# Revit family: QF_ELECTROLUXPROFESSIONAL_1L059Y_TD6-14_E
name_source: partatom
category: Attrezzature speciali
units: mm (PartAtom-declared; Revit-internal decimal feet)

## family parameters
Basato su piano di lavoro = No
Condiviso = No
Punto di calcolo locali = No
Quota connettore circolare = Usa diametro
Sempre verticale = Sì
Taglio con vuoti quando caricato = No
Tipo di parte = Normale

## types (85) — shared parameters
Depth Actual = 965 mm  [stored 3.16601 ft]
Height Actual = 1771 mm  [stored 5.81037 ft]
Latent Heat Output = 0.0
Length Actual = 790 mm  [stored 2.59186 ft]
Modello = TD6-14
Produttore = Electrolux Professional
Sensible Heat Output = 0.0
URL = www.electroluxprofessional.com
Weight = 222
zero-valued in all types: Gas KW, Prospetto di default, Steam Pounds per Hour

## per-type parameters (varying)
| type | Cycle | Descrizione | Item Number | Phase | Volts | Watts |
| 9873730095 | 50 Hz | TUMBLE DRYER TD6-14 MARINE 14KG SST DRUM EL 13,5KW 400/50/3N COMPASS PRO 6G81 EU SILVER DO.LEFT.INS. MB DSC AFC STOP DIS | 1LSNF8 | 3 | 400 V | 14500 W |
| 9873730045 | 60 Hz | TUMBLE DRYER TD6-14 MARINE 14KG GALVA.DRUM EL 9KW 440/60/3 COMPASS PRO 6G82 SE SILVER DO.LEFT STOP DISCON. | 1L0EFV | 3 | 440 V | 10000 W |
| 9873730065 | 50 Hz | TUMBLE DRYER TD6-14 14KG GALVA.DRUM EL 13,5KW 400/50/3N COMPASS PRO 6G81 EU SILVER DO.RIGHT MB STOP DISCON. | 1L80FS | 3 | 400 V | 14500 W |
| 9873730075 | 50 Hz | TUMBLE DRYER TD6-14 14KG SST DRUM EL 13,5KW 400/50/3 COMPASS PRO 6L80 EU SILVER DO.RIGHT EXT.PM. DISCON. 2.I/O | 1L80GL | 3 | 400 V | 14500 W |
| 9873730161 | 50 Hz | TUMBLE DRYER TD6-14 14KG SST DRUM EL 9KW 400/50/3 COMPASS PRO 6L80 EU SILVER DO.RIGHT ELS-NETW. DISCON. 2.I/O | 1L0GDJ | 3 | 400 V | 10000 W |
| 9873730210 | 50 Hz | TUMBLE DRYER TD6-14 14KG SST DRUM EL 13,5KW 230/50/3 COMPASS PRO 6G81 EU SILVER DO.RIGHT MB STOP DISCON. | 1L0HEK | 3 | 230 V | 14600 W |
| 9873730111 | 60 Hz | TUMBLE DRYER TD6-14 14KG SST DRUM EL 13,5KW 230/60/3 COMPASS PRO 6G82 EU SILVER DO.RIGHT STOP DISCON. | 1LSNR6 | 3 | 230 V | 14600 W |
| 9873730131 | 50 Hz | TUMBLE DRYER TD6-14 MARINE 14KG SST DRUM EL 13,5KW 400/50/3 COMPASS PRO 6G82 EU SILVER DO.RIGHT STOP DISCON. | 1L0G28 | 3 | 400 V | 14500 W |
| 9873730081 | 50 Hz | TUMBLE DRYER TD6-14 MARINE 14KG GALVA.DRUM EL 13,5KW 400/50/3 COMPASS PRO 6G82 EU SILVER DO.RIGHT STOP DISCON. | 1LSN4T | 3 | 400 V | 14500 W |
| 9873730091 | 60 Hz | TUMBLE DRYER TD6-14 MARINE 14KG SST DRUM EL 13,5KW 440/60/3 COMPASS PRO 6G82 EU SILVER DO.LEFT STOP DISCON. | 1L0ELU | 3 | 440 V | 14500 W |
| 9873730194 | 60 Hz | TUMBLE DRYER TD6-14 MARINE 14KG SST DRUM EL 13,5KW 480/60/3 COMPASS PRO 6G82 EU SST DO.LEFT STOP DISCON. EXT.CONN. | 1LSPPY | 3 | 480 V | 14500 W |
| 9873730061 | 50 Hz | TUMBLE DRYER TD6-14 14KG SST DRUM EL 13,5KW 230/50/3 COMPASS PRO 6G82 EU SILVER DO.RIGHT STOP DISCON. | 1L80EJ | 3 | 230 V | 14600 W |
| 9873730071 | 50 Hz | TUMBLE DRYER TD6-14 14KG GALVA.DRUM EL 6KW 230/50/1N COMPASS PRO 6G81 EU SILVER DO.RIGHT MB STOP DISCON. | 1L0EJ0 | 1 | 230 V | 7000 W |
| 9873730011 | 50 Hz | TUMBLE DRYER TD6-14 14KG GALVA.DRUM EL 9KW 400/50/3N COMPASS PRO 6A81 SE SILVER DO.LEFT.INS. MB DISCON. EXT.CONN. | 1L0EE0 | 3 | 400 V | 10000 W |
| 9873730021 | 60 Hz | TUMBLE DRYER TD6-14 14KG GALVA.DRUM EL 13,5KW 440/60/3 COMPASS PRO 6G82 EU SST/SILVER DO.RIGHT.INS. STOP DISCON. | 1LSN3B | 3 | 440 V | 14500 W |
| 9873730154 | 50 Hz | TUMBLE DRYER TD6-14 14KG SST DRUM EL 13,5KW 400/50/3N COMPASS PRO 6L80 EU SILVER DO.RIGHT EXT.PM. DISCON. 2.I/O | 1LSPA9 | 3 | 400 V | 14500 W |
| 9873730164 | 50 Hz | TUMBLE DRYER TD6-14 14KG GALVA.DRUM EL 13,5KW 400/50/3N COMPASS PRO 6G82 EU SILVER DO.RIGHT AFC STOP DISCON. | 1L0GF2 | 3 | 400 V | 14500 W |
| 9873730174 | 60 Hz | TUMBLE DRYER TD6-14 14KG GALVA.DRUM EL 13,5KW 440/60/3 COMPASS PRO 6L80 EU SILVER DO.RIGHT DISCON. | 1L0GPV | 3 | 440 V | 14500 W |
| 9873730104 | 60 Hz | TUMBLE DRYER TD6-14 MARINE 14KG GALVA.DRUM EL 13,5KW 230/60/3 COMPASS PRO 6G82 EU SST/SILVER DO.RIGHT STOP DISCON. | 1L0FYE | 3 | 230 V | 14600 W |
| 9873730114 | 50 Hz | TUMBLE DRYER TD6-14 14KG GALVA.DRUM EL 13,5KW 400/50/3N COMPASS PRO 6L80 EU SILVER DO.RIGHT DISCON. | 1LSNSA | 3 | 400 V | 14500 W |
| 9873730190 | 60 Hz | TUMBLE DRYER TD6-14 MARINE 14KG GALVA.DRUM EL 13,5KW 440/60/3 COMPASS PRO 6G82 SE SST/SILVER DO.LEFT STOP DISCON. EXT.CO | 1LSPPR | 3 | 440 V | 14500 W |
| 9873730140 | 50 Hz | TUMBLE DRYER TD6-14 14KG SST DRUM EL 13,5KW 400/50/3N COMPASS PRO 6G81 EU SST DO.RIGHT ELS-NETW. MB DSC AFC STOP DISCON. | 1LA09J | 3 | 400 V | 14500 W |
| 9873730100 | 50 Hz | TUMBLE DRYER TD6-14 14KG GALVA.DRUM EL 13,5KW 400/50/3N COMPASS PRO 6A81 SE SILVER DO.LEFT MB AFC | 1LSNGX | 3 | 400 V | 14500 W |
| 9873730089 | 60 Hz | TUMBLE DRYER TD6-14 MARINE 14KG GALVA.DRUM EL 13,5KW 230/60/3 COMPASS PRO 6G82 SE SILVER DO.LEFT STOP DISCON. | 1LSN8G | 3 | 230 V | 14600 W |
| 9873730099 | 50 Hz | TUMBLE DRYER TD6-14 14KG GALVA.DRUM EL 13,5KW 400/50/3N COMPASS PRO 6G81 EU SILVER DO.RIGHT MB AFC STOP DISCON. | 1LSNGW | 3 | 400 V | 14500 W |
| 9873730019 | 50 Hz | TUMBLE DRYER TD6-14 14KG GALVA.DRUM EL 13,5KW 400/50/3 COMPASS PRO 6G82 EU SILVER DO.RIGHT STOP DISCON. | 1LSN2G | 3 | 400 V | 14500 W |
| 9873730039 | 50 Hz | TUMBLE DRYER TD6-14 14KG GALVA.DRUM EL 13,5KW 400/50/3 COMPASS PRO 6G81 EU SILVER DO.RIGHT.INS. MB STOP DISCON. EXT.CONN | 1L0EE3 | 3 | 400 V | 14500 W |
| 9873730188 | 60 Hz | TUMBLE DRYER TD6-14 14KG GALVA.DRUM EL 9KW 230/60/3 COMPASS PRO 6G82 EU SILVER DO.RIGHT STOP DISCON. EXT.CONN. | 1LSPPT | 3 | 230 V | 10000 W |
| 9873730148 | 50 Hz | TUMBLE DRYER TD6-14 14KG SST DRUM EL 13,5KW 400/50/3N COMPASS PRO 6G81 EU SILVER DO.RIGHT.INS. MB STOP DISCON. | 1L0G9B | 3 | 400 V | 14500 W |
| 9873730168 | 50 Hz | TUMBLE DRYER TD6-14 14KG GALVA.DRUM EL 9KW 230/50/3 COMPASS PRO 6G81 EU SILVER DO.RIGHT MB STOP DISCON. | 1LA21U | 3 | 230 V | 10000 W |
| 9873730118 | 60 Hz | TUMBLE DRYER TD6-14 14KG GALVA.DRUM EL 13,5KW 400/60/3N COMPASS PRO 6G81 EU SILVER DO.RIGHT MB STOP DISCON. | 1LSNV3 | 3 | 400 V | 14500 W |
| 9873730205 | 50 Hz | TUMBLE DRYER TD6-14 14KG GALVA.DRUM EL 13,5KW 415/50/3N COMPASS PRO 6G81 EU SST/SILVER DO.LEFT MB DSC STOP DISCON. | 1L0HC3 | 3 | 415 V | 14500 W |
| 9873730096 | 60 Hz | TUMBLE DRYER TD6-14 14KG SST DRUM EL 13,5KW 400/60/3 COMPASS PRO 6G81 EU SILVER DO.RIGHT MB STOP DISCON. | 1LSNFX | 3 | 400 V | 14500 W |
| 9873730046 | 50 Hz | TUMBLE DRYER TD6-14 14KG SST DRUM EL 9KW 400/50/3N COMPASS PRO 6G81 EU SILVER DO.RIGHT MB STOP DISCON. | 1L0EG0 | 3 | 400 V | 10000 W |
| 9873730056 | 50 Hz | TUMBLE DRYER TD6-14 14KG GALVA.DRUM EL 9KW 230/50/3 COMPASS PRO 6G82 EU SILVER DO.RIGHT STOP DISCON. EXT.CONN. | 1L80DV | 3 | 230 V | 10000 W |
| 9873730066 | 50 Hz | TUMBLE DRYER TD6-14 14KG GALVA.DRUM EL 13,5KW 400/50/3N COMPASS PRO 6G81 EU SILVER DO.RIGHT MB STOP DISCON. EXT.CONN. | 1L80FT | 3 | 400 V | 14500 W |
| 9873730076 | 50 Hz | TUMBLE DRYER TD6-14 14KG GALVA.DRUM EL 13,5KW 400/50/3N COMPASS PRO 6A81 EU SILVER DO.RIGHT.INS. PREP.CB MB DISCON. 2.I/ | 1L80GM | 3 | 400 V | 14500 W |
| 9873730082 | 50 Hz | TUMBLE DRYER TD6-14 14KG GALVA.DRUM EL 13,5KW 400/50/3 COMPASS PRO 6L80 EU SILVER DO.RIGHT EXT.PM. DISCON. 2.I/O | 1LSN56 | 3 | 400 V | 14500 W |
| 9873730042 | 50 Hz | TUMBLE DRYER TD6-14 14KG GALVA.DRUM EL 13,5KW 230/50/3 COMPASS PRO 6G81 EU SILVER DO.RIGHT.INS. MB STOP DISCON. EXT.CONN | 1L0EET | 3 | 230 V | 14600 W |
| 9873730062 | 60 Hz | TUMBLE DRYER TD6-14 14KG SST DRUM EL 9KW 400/60/3 COMPASS PRO 6L80 EU SILVER DO.RIGHT EXT.PM. DISCON. 2.I/O | 1L80FA | 3 | 400 V | 10000 W |
| 9873730072 | 60 Hz | TUMBLE DRYER TD6-14 14KG SST DRUM EL 13,2KW 115/60/3 COMPASS PRO 6L80 EU SILVER DO.RIGHT EXT.PM. DISCON. 2.I/O | 1L0EJE | 3 | 115 V | 14200 W |
| 9873730012 | 50 Hz | TUMBLE DRYER TD6-14 14KG GALVA.DRUM EL 13,5KW 400/50/3N COMPASS PRO 6G81 EU SILVER DO.RIGHT.INS. MB STOP DISCON. EXT.CON | 1L0E90 | 3 | 400 V | 14500 W |
| 9873730022 | 50 Hz | TUMBLE DRYER TD6-14 14KG GALVA.DRUM EL 13,5KW 400/50/3N COMPASS PRO 6G81 EU SILVER DO.RIGHT ELS-NETW. MB STOP DISCON. EX | 1LSN2J | 3 | 400 V | 14500 W |
| 9873730157 | 50 Hz | TUMBLE DRYER TD6-14 14KG GALVA.DRUM EL 13,5KW 400/50/3N COMPASS PRO 6G82 EU SILVER DO.RIGHT STOP DISCON. | 1LSPAC | 3 | 400 V | 14500 W |
| 9873730212 | 50 Hz | TUMBLE DRYER TD6-14 14KG SST DRUM EL 6KW 230/50/1N COMPASS PRO 6G82 EU SILVER DO.RIGHT STOP DISCON. | 1LT6CJ | 1 | 230 V | 7000 W |
| 9873730117 | 50 Hz | TUMBLE DRYER TD6-14 14KG SST DRUM EL 13,5KW 400/50/3 COMPASS PRO 6L80 EU SILVER DO.RIGHT DISCON. | 1LSNSD | 3 | 400 V | 14500 W |
| 9873730222 | 50 Hz | TUMBLE DRYER TD6-14 MARINE 14KG SST DRUM EL 13,5KW 400/50/3N COMPASS PRO 6G81 EU SILVER DO.LEFT MB DSC STOP DISCON. | 1LT6T4 | 3 | 400 V | 14500 W |
| 9873730057 | 60 Hz | TUMBLE DRYER TD6-14 14KG GALVA.DRUM EL 13,5KW 230/60/3 COMPASS PRO 6G81 EU SILVER DO.RIGHT MB STOP DISCON. | 1L80DW | 3 | 230 V | 14600 W |
| 9873730207 | 50 Hz | TUMBLE DRYER TD6-14 MARINE 14KG GALVA.DRUM EL 6KW 230/50/1N COMPASS PRO 6G81 EU SST/SILVER DO.RIGHT MB STOP DISCON. | 1L82D1 | 1 | 230 V | 7000 W |
| 9873730217 | 50 Hz | TUMBLE DRYER TD6-14 14KG SST DRUM EL 13,5KW 400/50/3N COMPASS PRO 6G81 EU SST DO.LEFT.INS. MB STOP DISCON. EXT.CONN. | 1L0HH6 | 3 | 400 V | 14500 W |
| 9873730193 | 60 Hz | TUMBLE DRYER TD6-14 14KG GALVA.DRUM EL 13,5KW 480/60/3 COMPASS PRO 6G82 EU SILVER DO.LEFT ELS-NETW. STOP DISCON. EXT.CON | 1LSPPX | 3 | 480 V | 14500 W |
| 9873730153 | 50 Hz | TUMBLE DRYER TD6-14 14KG GALVA.DRUM EL 13,5KW 400/50/3N COMPASS PRO 6L80 EU SILVER DO.RIGHT EXT.PM. DISCON. 2.I/O | 1LSPA8 | 3 | 400 V | 14500 W |
| 9873730088 | 50 Hz | TUMBLE DRYER TD6-14 14KG SST DRUM EL 9KW 400/50/3 COMPASS PRO 6G81 EU SILVER DO.RIGHT MB STOP DISCON. | 1LSN84 | 3 | 400 V | 10000 W |
| 9873730133 | 50 Hz | TUMBLE DRYER TD6-14 14KG GALVA.DRUM EL 13,5KW 230/50/3 COMPASS PRO 6A81 EU SILVER DO.LEFT MB AFC DISCON. | 1LSNZG | 3 | 230 V | 14600 W |
| 9873730018 | 50 Hz | TUMBLE DRYER TD6-14 14KG GALVA.DRUM EL 9KW 400/50/3N COMPASS PRO 6A81 SE SILVER DO.LEFT.INS. MB DSC AFC DISCON. | 1L0E96 | 3 | 400 V | 14500 W |
| 9873730038 | 60 Hz | TUMBLE DRYER TD6-14 MARINE 14KG GALVA.DRUM EL 13,5KW 440/60/3 COMPASS PRO 6G82 EU SILVER DO.RIGHT STOP DISCON. | 1L0EE1 | 3 | 440 V | 14500 W |
| 9873730093 | 50 Hz | TUMBLE DRYER TD6-14 14KG SST DRUM EL 13,5KW 400/50/3 COMPASS PRO 6G81 EU SST/SILVER DO.LEFT MB STOP DISCON. | 1LSNBP | 3 | 400 V | 14500 W |
| 9873730073 | 60 Hz | TUMBLE DRYER TD6-14 MARINE 14KG SST DRUM EL 13,2KW 115/60/3 COMPASS PRO 6G82 EU SILVER DO.RIGHT STOP DISCON. | 1L0EJF | 3 | 115 V | 14200 W |
| 9873730146 | 50 Hz | TUMBLE DRYER TD6-14 14KG GALVA.DRUM EL 13,5KW 400/50/3N COMPASS PRO 6G81 EU SILVER DO.RIGHT MB STOP DISCON. EXT.CONN. | 1L0GB2 | 3 | 400 V | 14500 W |
| 9873730156 | 50 Hz | TUMBLE DRYER TD6-14 14KG SST DRUM EL 13,5KW 400/50/3N COMPASS PRO 6G82 EU SILVER DO.RIGHT STOP DISCON. | 1LSPAB | 3 | 400 V | 14500 W |
| 9873730106 | 50 Hz | TUMBLE DRYER TD6-14 14KG GALVA.DRUM EL 13,5KW 400/50/3N COMPASS PRO 6G81 EU SILVER DO.RIGHT.INS. MB DSC AFC STOP DISCON. | 1LSNN9 | 3 | 400 V | 14500 W |
| 9873730223 | 50 Hz | TUMBLE DRYER TD6-14 MARINE 14KG SST DRUM EL 13,5KW 400/50/3N COMPASS PRO 6G81 EU SILVER DO.LEFT.INS. MB DSC STOP DISCON. | 1LT6T5 | 3 | 400 V | 14500 W |
| 9873730126 | 60 Hz | TUMBLE DRYER TD6-14 MARINE 14KG SST DRUM EL 13,5KW 440/60/3 COMPASS PRO 6G81 EU SILVER DO.RIGHT MB STOP DISCON. | 1LSNY0 | 3 | 440 V | 14500 W |
| 9873730084 | 50 Hz | TUMBLE DRYER TD6-14 14KG GALVA.DRUM EL 13,5KW 400/50/3N COMPASS PRO 6A81 EU SILVER DO.LEFT.INS. ELS-NETW. PREP.CB MB DIS | 1LSN60 | 3 | 400 V | 14500 W |
| 9873730044 | 50 Hz | TUMBLE DRYER TD6-14 14KG GALVA.DRUM EL 9KW 400/50/3N COMPASS PRO 6A81 SE SILVER DO.LEFT MB EXT.CONN. | 1L0EFU | 3 | 400 V | 10000 W |
| 9873730054 | 60 Hz | TUMBLE DRYER TD6-14 MARINE 14KG GALVA.DRUM EL 13,5KW 440/60/3 COMPASS PRO 6G82 SE SST/SILVER DO.LEFT STOP DISCON. EXT.CO | 1L80DM | 3 | 440 V | 14500 W |
| 9873730074 | 50 Hz | TUMBLE DRYER TD6-14 14KG SST DRUM EL 13,5KW 400/50/3N COMPASS PRO 6G82 EU SILVER DO.RIGHT STOP DISCON. EXT.CONN. | 1L0EK1 | 3 | 400 V | 14500 W |
| 9873730159 | 50 Hz | TUMBLE DRYER TD6-14 MARINE 14KG SST DRUM EL 13,5KW 400/50/3 COMPASS PRO 6G82 SE SST DO.LEFT STOP DISCON. EXT.CONN. | 1LSPAW | 3 | 400 V | 14500 W |
| 9873730034 | 50 Hz | TUMBLE DRYER TD6-14 14KG GALVA.DRUM EL 6KW 230/50/1N COMPASS PRO 6G82 EU SILVER DO.RIGHT STOP DISCON. | 1LSN3A | 1 | 230 V | 7000 W |
| 9873730218 | 50 Hz | TUMBLE DRYER TD6-14 MARINE 14KG SST DRUM EL 13,5KW 415/50/3 COMPASS PRO 6G81 EU SST DO.RIGHT MB STOP DISCON. | 1L0HJ5 | 3 | 415 V | 14500 W |
| 9873730119 | 60 Hz | TUMBLE DRYER TD6-14 14KG GALVA.DRUM EL 13,5KW 400/60/3N COMPASS PRO 6G82 EU SILVER DO.RIGHT STOP DISCON. | 1LSNV4 | 3 | 400 V | 14500 W |
| 9873730129 | 50 Hz | TUMBLE DRYER TD6-14 14KG GALVA.DRUM EL 13,5KW 400/50/3N COMPASS PRO 6G81 EU SILVER DO.LEFT MB STOP DISCON. | 1L0G1U | 3 | 400 V | 14500 W |
| 9873730139 | 50 Hz | TUMBLE DRYER TD6-14 14KG SST DRUM EL 13,5KW 415/50/3N COMPASS PRO 6G81 EU SST DO.RIGHT.INS. MB STOP DISCON. | 1LSNZV | 3 | 415 V | 14500 W |
| 9873730179 | 60 Hz | TUMBLE DRYER TD6-14 14KG SST DRUM EL 13,5KW 208-240/60/3 COMPASS PRO 6G85 USA SST/SILVER DO.LEFT MB DISCON. | 1LSPJH | 3 | 240 V | 14500 W |
| 9873730182 | 50 Hz | TUMBLE DRYER TD6-14 14KG SST DRUM EL 13,5KW 400/50/3N COMPASS PRO 6G81 EU SILVER DO.RIGHT MB AFC STOP DISCON. | 1L0GYY | 3 | 400 V | 14500 W |
| 9873730192 | 60 Hz | TUMBLE DRYER TD6-14 MARINE 14KG GALVA.DRUM EL 13,5KW 480/60/3 COMPASS PRO 6G82 SE SST/SILVER DO.LEFT STOP DISCON. EXT.CO | 1LSPPW | 3 | 480 V | 14500 W |
| 9873730162 | 50 Hz | TUMBLE DRYER TD6-14 MARINE 14KG SST DRUM EL 13,5KW 400/50/3 COMPASS PRO 6G82 SE SST/SILVER DO.LEFT STOP DISCON. EXT.CONN | 1LSPBV | 3 | 400 V | 14500 W |
| 9873730112 | 50 Hz | TUMBLE DRYER TD6-14 14KG GALVA.DRUM EL 9KW 400/50/3N COMPASS PRO 6L80 EU SILVER DO.RIGHT DISCON. | 1LSNS8 | 3 | 400 V | 10000 W |
| 9873730080 | 50 Hz | TUMBLE DRYER TD6-14 14KG GALVA.DRUM EL 13,5KW 415/50/3N COMPASS PRO 6G82 EU SILVER DO.LEFT STOP DISCON. | 1L80H9 | 3 | 415 V | 14500 W |
| 9873730195 | 60 Hz | TUMBLE DRYER TD6-14 MARINE 14KG SST DRUM EL 13,5KW 480/60/3 COMPASS PRO 6G82 EU SST DO.RIGHT STOP DISCON. EXT.CONN. | 1LSPPZ | 3 | 480 V | 14500 W |
| 9873730070 | 50 Hz | TUMBLE DRYER TD6-14 MARINE 14KG GALVA.DRUM EL 13,5KW 400/50/3 COMPASS PRO 6G82 SE SST/SILVER DO.LEFT STOP DISCON. EXT.CO | 1L0EHZ | 3 | 400 V | 14500 W |
| 9873730145 | 50 Hz | TUMBLE DRYER TD6-14 14KG SST DRUM EL 13,5KW 400/50/3N COMPASS PRO 6G81 EU SILVER DO.RIGHT MB STOP DISCON. | 1LSP6T | 3 | 400 V | 14500 W |
| 9873730020 | 50 Hz | TUMBLE DRYER TD6-14 14KG SST DRUM EL 13,5KW 400/50/3 COMPASS PRO 6G81 EU SILVER DO.RIGHT MB STOP DISCON. | 1LSN2H | 3 | 400 V | 14500 W |
| 9873730030 | 50 Hz | TUMBLE DRYER TD6-14 14KG SST DRUM EL 13,5KW 400/50/3 COMPASS PRO 6G82 EU SILVER DO.RIGHT STOP DISCON. | 1L0EDA | 3 | 400 V | 14500 W |
| 9873730125 | 60 Hz | TUMBLE DRYER TD6-14 MARINE 14KG SST DRUM EL 13,5KW 440/60/3 COMPASS PRO 6G82 EU SST/SILVER DO.LEFT STOP DISCON. | 1LSNXL | 3 | 440 V | 14500 W |

note: [stored X ft] marks values corroborated as IEEE doubles in the binary element streams (Revit-internal decimal feet)

## geometry (parser evidence)
native form markers: Blend x8
no freeform markers — native parametric forms only
